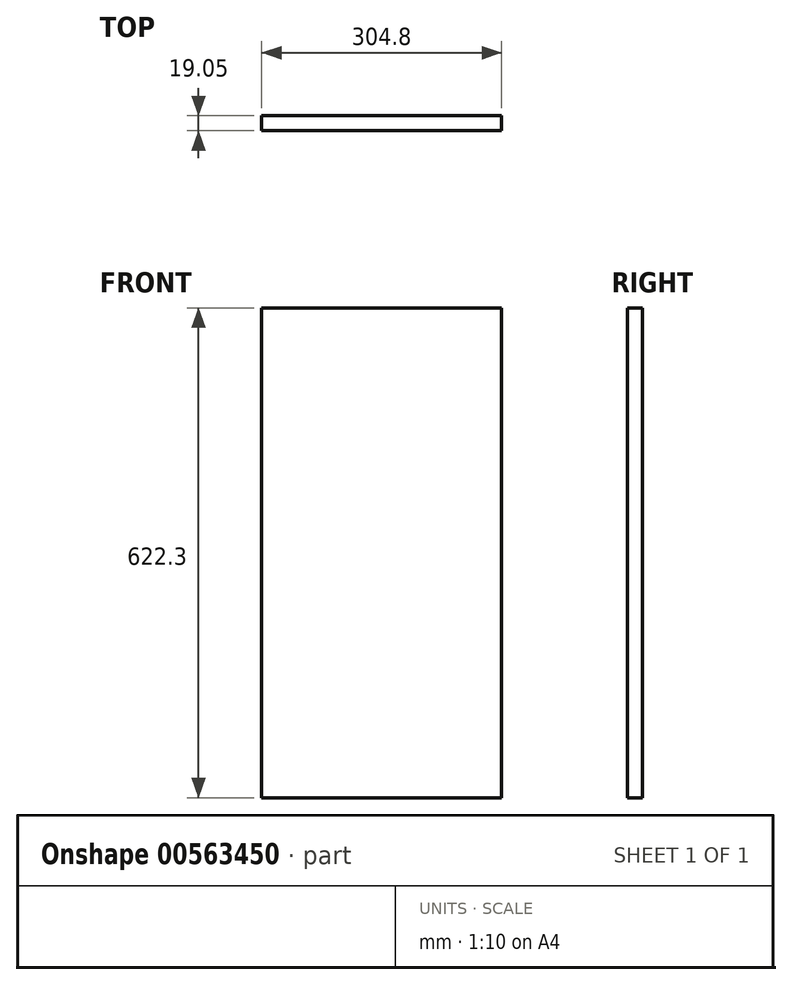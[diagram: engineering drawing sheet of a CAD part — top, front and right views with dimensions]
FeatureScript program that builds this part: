
annotation { "Feature Type Name" : "Feature", "Feature Type Description" : "" }
export const myFeature = defineFeature(function(context is Context, id is Id, definition is map)
    precondition{}
    {
        {
            var Q0;
            Q0=qCreatedBy(makeId("Top.planeOp"),FACE);
            var sketch = newSketch(context, id + "F0", { "sketchPlane" : qUnion([Q0])});
            skLineSegment(sketch, "E0.bottom", {"start": v(-128.23, -20.33) * mm, "end": v(176.57, -20.33) * mm});
            skLineSegment(sketch, "E0.top", {"start": v(-128.23, -39.38) * mm, "end": v(176.57, -39.38) * mm});
            skLineSegment(sketch, "E0.left", {"start": v(-128.23, -20.33) * mm, "end": v(-128.23, -39.38) * mm});
            skLineSegment(sketch, "E0.right", {"start": v(176.57, -20.33) * mm, "end": v(176.57, -39.38) * mm});
            skSolve(sketch);
        }
        {
            var Q0;
            Q0=qSketchRegion(id+"F0",true);
            extrude(context, id + "F1", {"entities" : qUnion([Q0]), "depth" : 622.3 * mm, "offsetDistance" : 25.4 * mm});
        }
    });
